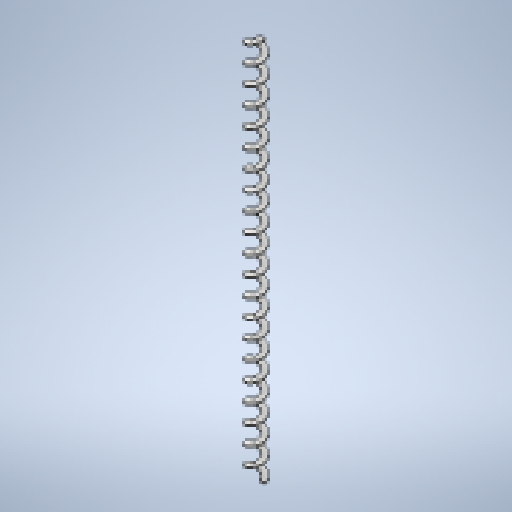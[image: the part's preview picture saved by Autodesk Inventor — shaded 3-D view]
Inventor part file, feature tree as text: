
AUTODESK INVENTOR PART (.ipt)
format: ipt  version: 2025.1 (Build 291241020, 241B)  size: 350,208 bytes
history: native  units: mm
features: helix x1, sketch x1
ambient origin geometry x8: Origin, YZ Plane, XZ Plane, XY Plane, X Axis, Y Axis, Z Axis, Center Point
bodies: Solid1 (feature_tree)
feature tree (2):
  helix  "Coil1"  [1 undecoded]
  sketch  "Sketch2"  dims[d3=90.0mm d4=10.0mm d5=210.0mm d6=0.0mm d7=90.0deg d8=90.0deg d9=0.0mm d10=0.0mm d11=30.0mm d12=90.0mm]
note: 1 required parameter value undecoded (feature->parameter linkage not recoverable at this tier; creation-order binding heuristic only, values carry confidence <= 0.55)
